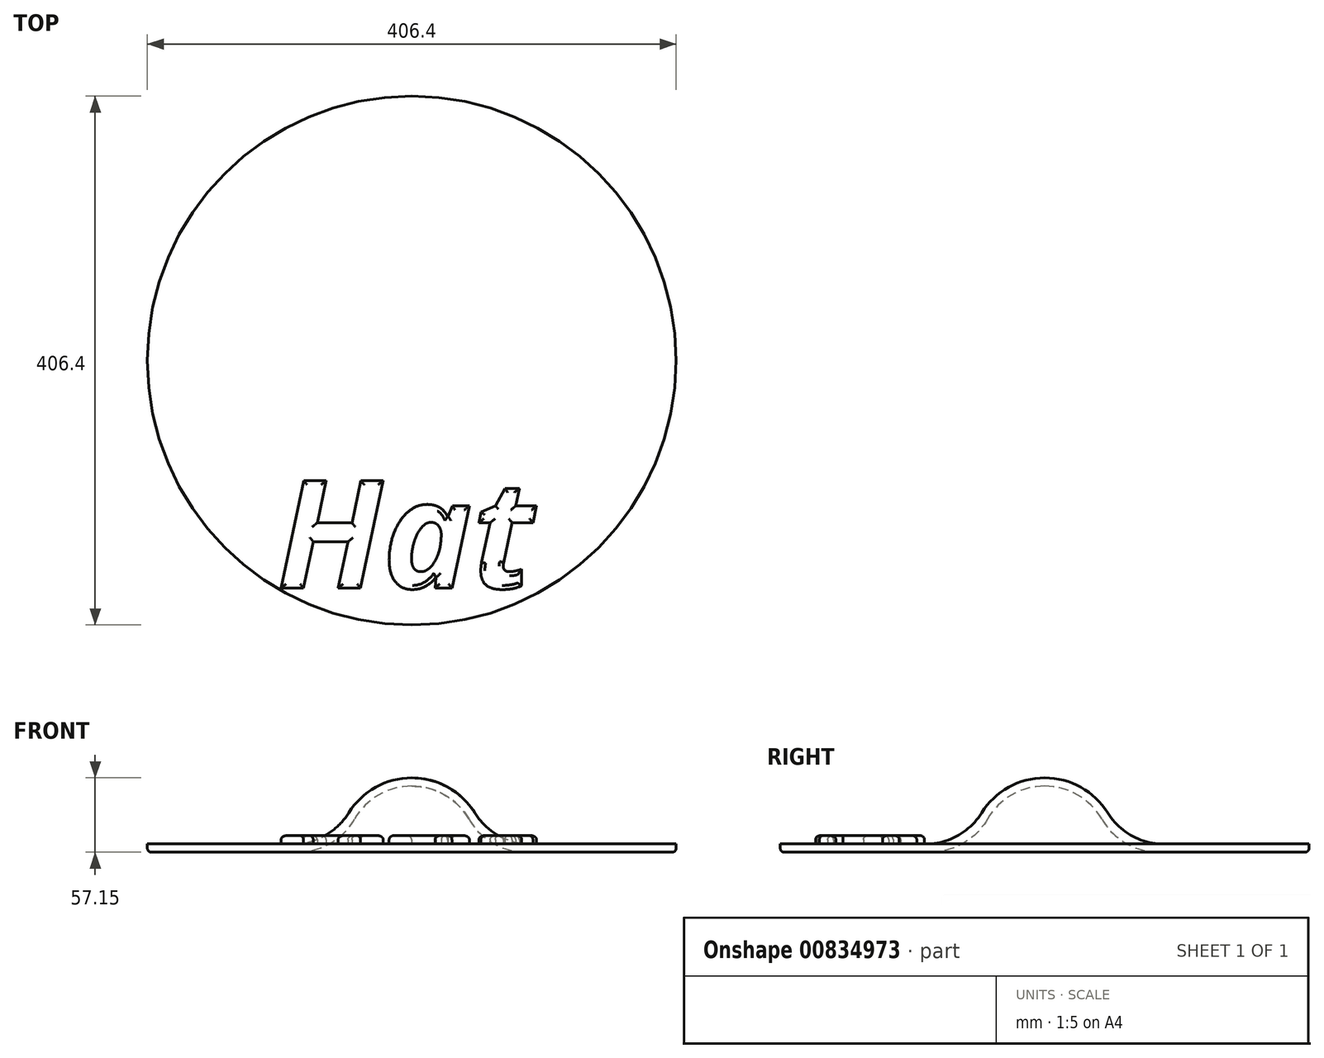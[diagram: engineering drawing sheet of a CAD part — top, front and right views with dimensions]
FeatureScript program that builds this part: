
annotation { "Feature Type Name" : "Feature", "Feature Type Description" : "" }
export const myFeature = defineFeature(function(context is Context, id is Id, definition is map)
    precondition{}
    {
        {
            var Q0;
            Q0=qCreatedBy(makeId("Front.planeOp"),FACE);
            var sketch = newSketch(context, id + "F0", { "sketchPlane" : qUnion([Q0])});
            skLineSegment(sketch, "E0", {"start": v(203.2, 0) * mm, "end": v(203.2, -6.35) * mm});
            skLineSegment(sketch, "E1", {"start": v(0, 44.45) * mm, "end": v(0, 50.8) * mm});
            skLineSegment(sketch, "E2", {"start": v(203.2, -6.35) * mm, "end": v(87.99, -6.35) * mm});
            skArc(sketch, "E3", {"start": v(0, 50.8) * mm, "mid": v(27.72, 43.63) * mm, "end": v(48.48, 23.9) * mm});
            skArc(sketch, "E4", {"start": v(0, 44.45) * mm, "mid": v(25.4, 37.64) * mm, "end": v(44, 19.05) * mm});
            skLineSegment(sketch, "E5", {"start": v(91.58, 0) * mm, "end": v(203.2, 0) * mm});
            skPoint(sketch, "E6.visualSharp", {"position": v(56.8, 0) * mm});
            skArc(sketch, "E6.filletArc", {"start": v(48.48, 23.9) * mm, "mid": v(66.94, 6.38) * mm, "end": v(91.58, 0) * mm});
            skPoint(sketch, "E7.visualSharp", {"position": v(50.8, -6.35) * mm});
            skArc(sketch, "E7.filletArc", {"start": v(44, 19.05) * mm, "mid": v(62.59, 0.46) * mm, "end": v(87.99, -6.35) * mm});
            skSolve(sketch);
        }
        {
            var Q0;
            Q0=makeQuery(id+"F0.imprint","IMPRINT",FACE,{"disambiguationData":[TD([[makeQuery(id+"F0.imprint","IMPRINT",EDGE,{"derivedFrom":sQuery(id+"F0.wireOp",EDGE,"S9fr5i61-g3Xa-egJd-yCp4-iOuRNOAeters")}),1.0]])]});
            var Q1;
            Q1=makeQuery(id+"F0.imprint","IMPRINT",FACE,{"disambiguationData":[TD([[makeQuery(id+"F0.imprint","IMPRINT",EDGE,{"derivedFrom":sQuery(id+"F0.wireOp",EDGE,"E0")}),-1.0]])]});
            var Q2;
            Q2=sQuery(id+"F0.wireOp",EDGE,"E1");
            revolve(context, id + "F1", {"surfaceOperationType" : NewSurfaceOperationType.NEW, "entities" : qUnion([Q0, Q1]), "axis" : qUnion([Q2]), "revolveType" : RevolveType.FULL});
        }
        {
            var Q0;
            Q0=makeQuery(id+"F1.opRevolve","SWEPT_FACE",FACE,{"disambiguationData":[OSD([sQuery(id+"F0.wireOp",EDGE,"E5")])]});
            var sketch = newSketch(context, id + "F2", { "sketchPlane" : qUnion([Q0])});
            skText(sketch, "E8", { "text": "Hat", "fontName": "OpenSans-BoldItalic.ttf"});
            const initialGuessF2  = {"E8": [-0.10346, -0.17489, 1, 0, 0.0833]};
            skSetInitialGuess(sketch, initialGuessF2);
            skSolve(sketch);
        }
        {
            var Q0;
            Q0 = qSketchRegion(id + "F2", true);
            extrude(context, id + "F3", {"entities" : qUnion([Q0]), "operationType" : NewBodyOperationType.ADD, "depth" : 6.35 * mm, "offsetDistance" : 25.4 * mm});
        }
        {
            var Q0;
            Q0=makeQuery(id+"F3.opExtrude","CAP_FACE",FACE,{"disambiguationData":[OSD([sQuery(id+"F2.wireOp",EDGE,"E8.sketch_text.stroke-0"),sQuery(id+"F2.wireOp",EDGE,"E8.sketch_text.stroke-1"),sQuery(id+"F2.wireOp",EDGE,"E8.sketch_text.stroke-2"),sQuery(id+"F2.wireOp",EDGE,"E8.sketch_text.stroke-3"),sQuery(id+"F2.wireOp",EDGE,"E8.sketch_text.stroke-4"),sQuery(id+"F2.wireOp",EDGE,"E8.sketch_text.stroke-5"),sQuery(id+"F2.wireOp",EDGE,"E8.sketch_text.stroke-6"),sQuery(id+"F2.wireOp",EDGE,"E8.sketch_text.stroke-7"),sQuery(id+"F2.wireOp",EDGE,"E8.sketch_text.stroke-8"),sQuery(id+"F2.wireOp",EDGE,"E8.sketch_text.stroke-9"),sQuery(id+"F2.wireOp",EDGE,"E8.sketch_text.stroke-10"),sQuery(id+"F2.wireOp",EDGE,"E8.sketch_text.stroke-11")])],"isStart":false});
            var Q1;
            Q1=makeQuery(id+"F3.opExtrude","CAP_FACE",FACE,{"disambiguationData":[OSD([sQuery(id+"F2.wireOp",EDGE,"E8.sketch_text.stroke-12"),sQuery(id+"F2.wireOp",EDGE,"E8.sketch_text.stroke-13"),sQuery(id+"F2.wireOp",EDGE,"E8.sketch_text.stroke-14"),sQuery(id+"F2.wireOp",EDGE,"E8.sketch_text.stroke-15"),sQuery(id+"F2.wireOp",EDGE,"E8.sketch_text.stroke-16"),sQuery(id+"F2.wireOp",EDGE,"E8.sketch_text.stroke-17"),sQuery(id+"F2.wireOp",EDGE,"E8.sketch_text.stroke-18"),sQuery(id+"F2.wireOp",EDGE,"E8.sketch_text.stroke-19"),sQuery(id+"F2.wireOp",EDGE,"E8.sketch_text.stroke-20"),sQuery(id+"F2.wireOp",EDGE,"E8.sketch_text.stroke-21"),sQuery(id+"F2.wireOp",EDGE,"E8.sketch_text.stroke-22"),sQuery(id+"F2.wireOp",EDGE,"E8.sketch_text.stroke-23"),sQuery(id+"F2.wireOp",EDGE,"E8.sketch_text.stroke-24"),sQuery(id+"F2.wireOp",EDGE,"E8.sketch_text.stroke-25"),sQuery(id+"F2.wireOp",EDGE,"E8.sketch_text.stroke-26"),sQuery(id+"F2.wireOp",EDGE,"E8.sketch_text.stroke-27"),sQuery(id+"F2.wireOp",EDGE,"E8.sketch_text.stroke-28"),sQuery(id+"F2.wireOp",EDGE,"E8.sketch_text.stroke-29"),sQuery(id+"F2.wireOp",EDGE,"E8.sketch_text.stroke-30"),sQuery(id+"F2.wireOp",EDGE,"E8.sketch_text.stroke-31"),sQuery(id+"F2.wireOp",EDGE,"E8.sketch_text.stroke-32"),sQuery(id+"F2.wireOp",EDGE,"E8.sketch_text.stroke-33"),sQuery(id+"F2.wireOp",EDGE,"E8.sketch_text.stroke-34"),sQuery(id+"F2.wireOp",EDGE,"E8.sketch_text.stroke-35"),sQuery(id+"F2.wireOp",EDGE,"E8.sketch_text.stroke-36")])],"isStart":false});
            var Q2;
            Q2=makeQuery(id+"F3.opExtrude","CAP_FACE",FACE,{"disambiguationData":[OSD([sQuery(id+"F2.wireOp",EDGE,"E8.sketch_text.stroke-37"),sQuery(id+"F2.wireOp",EDGE,"E8.sketch_text.stroke-38"),sQuery(id+"F2.wireOp",EDGE,"E8.sketch_text.stroke-39"),sQuery(id+"F2.wireOp",EDGE,"E8.sketch_text.stroke-40"),sQuery(id+"F2.wireOp",EDGE,"E8.sketch_text.stroke-41"),sQuery(id+"F2.wireOp",EDGE,"E8.sketch_text.stroke-42"),sQuery(id+"F2.wireOp",EDGE,"E8.sketch_text.stroke-43"),sQuery(id+"F2.wireOp",EDGE,"E8.sketch_text.stroke-44"),sQuery(id+"F2.wireOp",EDGE,"E8.sketch_text.stroke-45"),sQuery(id+"F2.wireOp",EDGE,"E8.sketch_text.stroke-46"),sQuery(id+"F2.wireOp",EDGE,"E8.sketch_text.stroke-47"),sQuery(id+"F2.wireOp",EDGE,"E8.sketch_text.stroke-48"),sQuery(id+"F2.wireOp",EDGE,"E8.sketch_text.stroke-49"),sQuery(id+"F2.wireOp",EDGE,"E8.sketch_text.stroke-50"),sQuery(id+"F2.wireOp",EDGE,"E8.sketch_text.stroke-51"),sQuery(id+"F2.wireOp",EDGE,"E8.sketch_text.stroke-52"),sQuery(id+"F2.wireOp",EDGE,"E8.sketch_text.stroke-53"),sQuery(id+"F2.wireOp",EDGE,"E8.sketch_text.stroke-54"),sQuery(id+"F2.wireOp",EDGE,"E8.sketch_text.stroke-55")])],"isStart":false});
            var Q3;
            Q3=makeQuery(id+"F1.opRevolve","SWEPT_EDGE",EDGE,{"disambiguationData":[OSD([sQuery(id+"F0.wireOp",EDGE,"E0"),sQuery(id+"F0.wireOp",EDGE,"E2")])]});
            fillet(context, id + "F4", {"entities" : qUnion([Q0, Q1, Q2, Q3]), "radius" : 3.17 * mm, "tangentPropagation" : true, "allowEdgeOverflow" : false});
        }
    });
